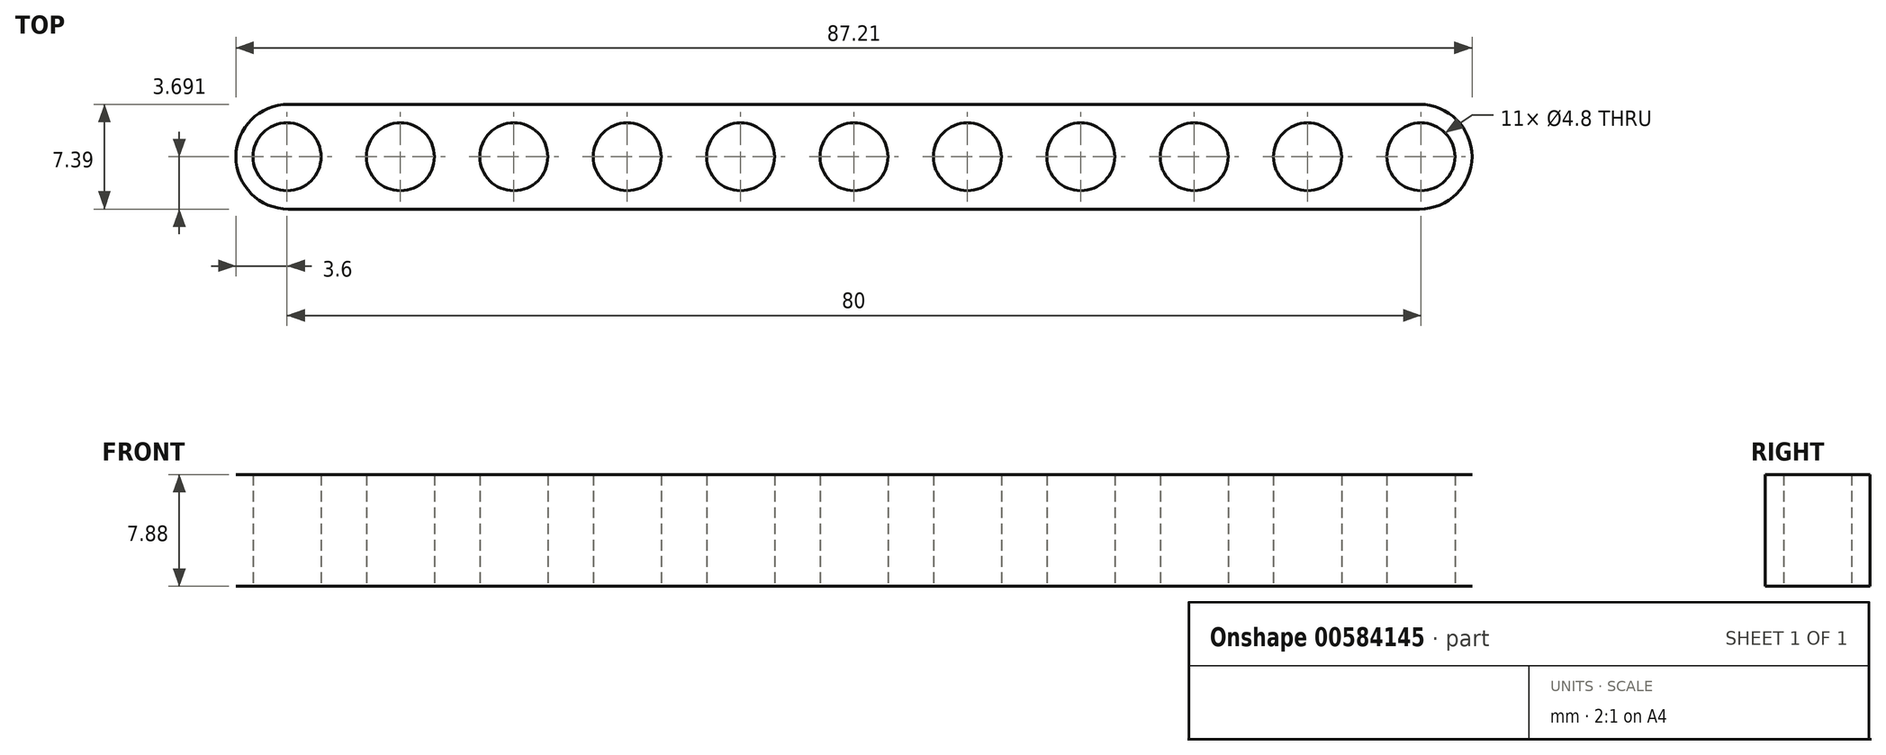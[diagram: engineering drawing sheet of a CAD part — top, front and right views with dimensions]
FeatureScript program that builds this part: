
annotation { "Feature Type Name" : "Feature", "Feature Type Description" : "" }
export const myFeature = defineFeature(function(context is Context, id is Id, definition is map)
    precondition{}
    {
        {
            var Q0;
            Q0=qCreatedBy(makeId("Top.planeOp"),FACE);
            var sketch = newSketch(context, id + "F0", { "sketchPlane" : qUnion([Q0])});
            skLineSegment(sketch, "E0", {"start": v(-28.72, 9.1) * mm, "end": v(-28.72, -19.18) * mm, "construction": true});
            skLineSegment(sketch, "E1", {"start": v(-28.72, -19.18) * mm, "end": v(-29.11, -19.18) * mm, "construction": true});
            skLineSegment(sketch, "E2", {"start": v(-1.18, -2.09) * mm, "end": v(-47.58, -2.09) * mm, "construction": true});
            skLineSegment(sketch, "E3", {"start": v(-47.58, -2.09) * mm, "end": v(-47.58, -1.54) * mm, "construction": true});
            skLineSegment(sketch, "E4", {"start": v(-28.72, 1.6) * mm, "end": v(-72.32, 1.6) * mm});
            skLineSegment(sketch, "E5", {"start": v(-72.32, 1.6) * mm, "end": v(-72.32, -2.09) * mm});
            skArc(sketch, "E6", {"start": v(-28.72, 0.31) * mm, "mid": v(-31.12, -2.09) * mm, "end": v(-28.72, -4.49) * mm});
            skCircle(sketch, "E7", {"center": v(-36.72, -2.09) * mm, "radius": 2.4 * mm});
            skCircle(sketch, "E8.1.0.0", {"center": v(-44.72, -2.09) * mm, "radius": 2.4 * mm});
            skLineSegment(sketch, "E8.direction1", {"start": v(-36.72, -2.09) * mm, "end": v(-44.72, -2.09) * mm, "construction": true});
            skCircle(sketch, "E9.0.2.0", {"center": v(-52.72, -2.09) * mm, "radius": 2.4 * mm});
            skCircle(sketch, "E9.0.3.0", {"center": v(-60.72, -2.09) * mm, "radius": 2.4 * mm});
            skCircle(sketch, "E9.0.4.0", {"center": v(-68.72, -2.09) * mm, "radius": 2.4 * mm});
            skLineSegment(sketch, "E10.MirrorCS", {"start": v(-28.72, -5.78) * mm, "end": v(-72.32, -5.78) * mm});
            skLineSegment(sketch, "E11.MirrorCS", {"start": v(-72.32, -5.78) * mm, "end": v(-72.32, -2.09) * mm});
            skLineSegment(sketch, "E12.MirrorCS", {"start": v(-9.86, -2.09) * mm, "end": v(-9.86, -1.54) * mm, "construction": true});
            skLineSegment(sketch, "E13.MirrorCS", {"start": v(-56.26, -2.09) * mm, "end": v(-9.86, -2.09) * mm, "construction": true});
            skArc(sketch, "E14.MirrorCS", {"start": v(-28.72, 0.31) * mm, "mid": v(-26.32, -2.09) * mm, "end": v(-28.72, -4.49) * mm});
            skCircle(sketch, "E15.MirrorC", {"center": v(-20.72, -2.09) * mm, "radius": 2.4 * mm});
            skCircle(sketch, "E16.MirrorC", {"center": v(-12.72, -2.09) * mm, "radius": 2.4 * mm});
            skLineSegment(sketch, "E17.MirrorCS", {"start": v(-28.72, 1.6) * mm, "end": v(14.89, 1.6) * mm});
            skLineSegment(sketch, "E18.MirrorCS", {"start": v(14.89, 1.6) * mm, "end": v(14.89, -2.09) * mm});
            skLineSegment(sketch, "E19.MirrorCS", {"start": v(14.89, -5.78) * mm, "end": v(14.89, -2.09) * mm});
            skLineSegment(sketch, "E20.MirrorCS", {"start": v(-28.72, -5.78) * mm, "end": v(14.89, -5.78) * mm});
            skCircle(sketch, "E21.MirrorC", {"center": v(-4.72, -2.09) * mm, "radius": 2.4 * mm});
            skLineSegment(sketch, "E22.MirrorCS", {"start": v(-20.72, -2.09) * mm, "end": v(-12.72, -2.09) * mm, "construction": true});
            skCircle(sketch, "E23.MirrorC", {"center": v(11.28, -2.09) * mm, "radius": 2.4 * mm});
            skCircle(sketch, "E24.MirrorC", {"center": v(3.28, -2.09) * mm, "radius": 2.4 * mm});
            skSolve(sketch);
        }
        {
            var Q0;
            Q0=makeQuery(id+"F0.imprint","IMPRINT",FACE,{"disambiguationData":[TD([[makeQuery(id+"F0.imprint","IMPRINT",EDGE,{"derivedFrom":sQuery(id+"F0.wireOp",EDGE,"E4")}),1.0]])]});
            extrude(context, id + "F1", {"entities" : qUnion([Q0]), "depth" : 7.88 * mm, "offsetDistance" : 25 * mm});
        }
        {
            var Q0;
            Q0=makeQuery(id+"F1.opExtrude","SWEPT_EDGE",EDGE,{"disambiguationData":[OSD([sQuery(id+"F0.wireOp",EDGE,"E17.MirrorCS"),sQuery(id+"F0.wireOp",EDGE,"E18.MirrorCS")])]});
            var Q1;
            Q1=makeQuery(id+"F1.opExtrude","SWEPT_EDGE",EDGE,{"disambiguationData":[OSD([sQuery(id+"F0.wireOp",EDGE,"E19.MirrorCS"),sQuery(id+"F0.wireOp",EDGE,"E20.MirrorCS")])]});
            var Q2;
            Q2=makeQuery(id+"F1.opExtrude","SWEPT_EDGE",EDGE,{"disambiguationData":[OSD([sQuery(id+"F0.wireOp",EDGE,"E4"),sQuery(id+"F0.wireOp",EDGE,"E5")])]});
            var Q3;
            Q3=makeQuery(id+"F1.opExtrude","SWEPT_EDGE",EDGE,{"disambiguationData":[OSD([sQuery(id+"F0.wireOp",EDGE,"E10.MirrorCS"),sQuery(id+"F0.wireOp",EDGE,"E11.MirrorCS")])]});
            fillet(context, id + "F2", {"entities" : qUnion([Q0, Q1, Q2, Q3]), "radius" : 3.7 * mm, "tangentPropagation" : true, "allowEdgeOverflow" : false});
        }
    });
